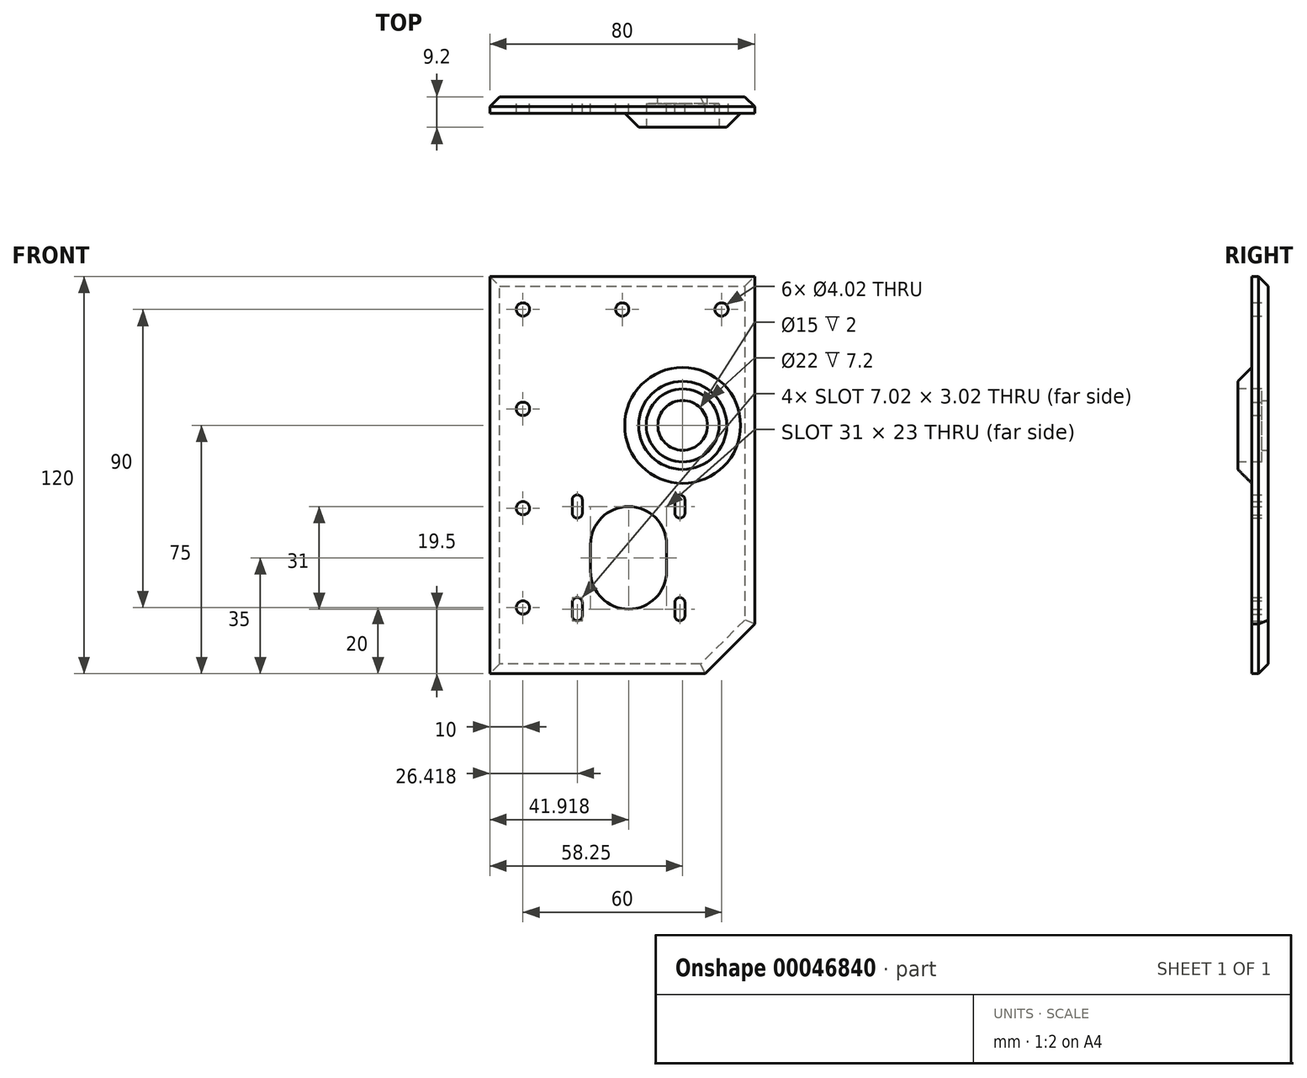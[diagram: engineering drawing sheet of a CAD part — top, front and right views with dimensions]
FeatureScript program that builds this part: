
annotation { "Feature Type Name" : "Feature", "Feature Type Description" : "" }
export const myFeature = defineFeature(function(context is Context, id is Id, definition is map)
    precondition{}
    {
        {
            var Q0;
            Q0=qCreatedBy(makeId("Front.planeOp"),FACE);
            var sketch = newSketch(context, id + "F0", { "sketchPlane" : qUnion([Q0])});
            skLineSegment(sketch, "E0", {"start": v(0, 0) * mm, "end": v(0, 70) * mm});
            skLineSegment(sketch, "E1", {"start": v(0, 70) * mm, "end": v(80, 70) * mm});
            skPoint(sketch, "E2.endSnap0", {"position": v(0, 35) * mm});
            skCircle(sketch, "E3", {"center": v(58.25, 25) * mm, "radius": 7.5 * mm});
            skLineSegment(sketch, "E4", {"start": v(80, 70) * mm, "end": v(80, -35) * mm});
            skLineSegment(sketch, "E5", {"start": v(65, -50) * mm, "end": v(0, -50) * mm});
            skLineSegment(sketch, "E6", {"start": v(0, -50) * mm, "end": v(0, 0) * mm});
            skLineSegment(sketch, "E7", {"start": v(65, -50) * mm, "end": v(80, -35) * mm});
            skLineSegment(sketch, "E8", {"start": v(20, 50) * mm, "end": v(20, -50) * mm, "construction": true});
            skLineSegment(sketch, "E9", {"start": v(20, 50) * mm, "end": v(80, 50) * mm, "construction": true});
            skCircle(sketch, "E10", {"center": v(41.92, -15) * mm, "radius": 11.5 * mm, "construction": true});
            skLineSegment(sketch, "E11", {"start": v(41.92, -15) * mm, "end": v(41.92, 0.5) * mm, "construction": true});
            skLineSegment(sketch, "E12", {"start": v(41.92, 0.5) * mm, "end": v(57.42, 0.5) * mm, "construction": true});
            skLineSegment(sketch, "E13", {"start": v(41.92, 0.5) * mm, "end": v(26.42, 0.5) * mm, "construction": true});
            skLineSegment(sketch, "E14", {"start": v(26.42, 0.5) * mm, "end": v(26.42, -15) * mm, "construction": true});
            skLineSegment(sketch, "E15", {"start": v(26.42, -15) * mm, "end": v(41.92, -15) * mm, "construction": true});
            skLineSegment(sketch, "E16", {"start": v(26.42, -15) * mm, "end": v(26.42, -30.5) * mm, "construction": true});
            skLineSegment(sketch, "E17", {"start": v(26.42, -30.5) * mm, "end": v(41.92, -30.5) * mm, "construction": true});
            skLineSegment(sketch, "E18", {"start": v(41.92, -30.5) * mm, "end": v(41.92, -15) * mm, "construction": true});
            skLineSegment(sketch, "E19", {"start": v(41.92, -15) * mm, "end": v(57.42, -15) * mm, "construction": true});
            skLineSegment(sketch, "E20", {"start": v(57.42, -15) * mm, "end": v(57.42, -30.5) * mm, "construction": true});
            skLineSegment(sketch, "E21", {"start": v(57.42, -30.5) * mm, "end": v(41.92, -30.5) * mm, "construction": true});
            skLineSegment(sketch, "E22", {"start": v(57.42, 0.5) * mm, "end": v(57.42, -15) * mm, "construction": true});
            skLineSegment(sketch, "E23", {"start": v(26.42, 0.5) * mm, "end": v(26.42, 5.5) * mm, "construction": true});
            skLineSegment(sketch, "E24", {"start": v(26.42, 0.5) * mm, "end": v(21.42, 0.5) * mm, "construction": true});
            skLineSegment(sketch, "E25", {"start": v(57.42, 0.5) * mm, "end": v(57.42, 5.5) * mm, "construction": true});
            skLineSegment(sketch, "E26", {"start": v(57.42, 0.5) * mm, "end": v(62.42, 0.5) * mm, "construction": true});
            skLineSegment(sketch, "E27", {"start": v(57.42, -30.5) * mm, "end": v(57.42, -35.5) * mm, "construction": true});
            skLineSegment(sketch, "E28", {"start": v(57.42, -30.5) * mm, "end": v(62.42, -30.5) * mm, "construction": true});
            skLineSegment(sketch, "E29", {"start": v(26.42, -30.5) * mm, "end": v(21.42, -30.5) * mm, "construction": true});
            skLineSegment(sketch, "E30", {"start": v(26.42, -30.5) * mm, "end": v(26.42, -35.5) * mm, "construction": true});
            skArc(sketch, "E31", {"start": v(58.93, -28.5) * mm, "mid": v(57.42, -26.99) * mm, "end": v(55.9, -28.5) * mm});
            skArc(sketch, "E32", {"start": v(55.9, -1.5) * mm, "mid": v(57.42, -3) * mm, "end": v(58.93, -1.5) * mm});
            skArc(sketch, "E33", {"start": v(24.9, -1.5) * mm, "mid": v(26.42, -3) * mm, "end": v(27.93, -1.5) * mm});
            skArc(sketch, "E34", {"start": v(27.93, -28.5) * mm, "mid": v(26.42, -26.99) * mm, "end": v(24.9, -28.5) * mm});
            skArc(sketch, "E35", {"start": v(24.9, -32.5) * mm, "mid": v(26.42, -34) * mm, "end": v(27.93, -32.5) * mm});
            skArc(sketch, "E36", {"start": v(55.9, -32.5) * mm, "mid": v(57.42, -34) * mm, "end": v(58.93, -32.5) * mm});
            skArc(sketch, "E37", {"start": v(58.93, 2.5) * mm, "mid": v(57.42, 4.01) * mm, "end": v(55.9, 2.5) * mm});
            skArc(sketch, "E38", {"start": v(27.93, 2.5) * mm, "mid": v(26.42, 4.01) * mm, "end": v(24.9, 2.5) * mm});
            skArc(sketch, "E39", {"start": v(53.42, -11) * mm, "mid": v(41.92, 0.5) * mm, "end": v(30.42, -11) * mm});
            skCircle(sketch, "E40", {"center": v(10, 60) * mm, "radius": 2 * mm});
            skCircle(sketch, "E41", {"center": v(40, 60) * mm, "radius": 2 * mm});
            skCircle(sketch, "E42", {"center": v(70, 60) * mm, "radius": 2 * mm});
            skCircle(sketch, "E43", {"center": v(10, 30) * mm, "radius": 2 * mm});
            skCircle(sketch, "E44", {"center": v(10, 0) * mm, "radius": 2 * mm});
            skCircle(sketch, "E45", {"center": v(10, -30) * mm, "radius": 2 * mm});
            skLineSegment(sketch, "E46", {"start": v(26.42, 2.5) * mm, "end": v(27.93, 2.5) * mm, "construction": true});
            skLineSegment(sketch, "E47", {"start": v(27.93, 2.5) * mm, "end": v(27.93, -1.5) * mm});
            skLineSegment(sketch, "E48", {"start": v(27.93, -1.5) * mm, "end": v(26.42, -1.5) * mm, "construction": true});
            skLineSegment(sketch, "E49", {"start": v(26.42, -1.5) * mm, "end": v(24.9, -1.5) * mm, "construction": true});
            skLineSegment(sketch, "E50", {"start": v(24.9, -1.5) * mm, "end": v(24.9, 2.5) * mm});
            skLineSegment(sketch, "E51", {"start": v(24.9, 2.5) * mm, "end": v(26.42, 2.5) * mm, "construction": true});
            skLineSegment(sketch, "E52", {"start": v(57.42, 2.5) * mm, "end": v(55.9, 2.5) * mm, "construction": true});
            skLineSegment(sketch, "E53", {"start": v(55.9, 2.5) * mm, "end": v(55.9, -1.5) * mm});
            skLineSegment(sketch, "E54", {"start": v(55.9, -1.5) * mm, "end": v(57.42, -1.5) * mm, "construction": true});
            skLineSegment(sketch, "E55", {"start": v(57.42, -1.5) * mm, "end": v(58.93, -1.5) * mm, "construction": true});
            skLineSegment(sketch, "E56", {"start": v(58.93, -1.5) * mm, "end": v(58.93, 2.5) * mm});
            skLineSegment(sketch, "E57", {"start": v(58.93, 2.5) * mm, "end": v(57.42, 2.5) * mm, "construction": true});
            skLineSegment(sketch, "E58", {"start": v(57.42, -32.5) * mm, "end": v(58.93, -32.5) * mm, "construction": true});
            skLineSegment(sketch, "E59", {"start": v(58.93, -32.5) * mm, "end": v(58.93, -28.5) * mm});
            skLineSegment(sketch, "E60", {"start": v(58.93, -28.5) * mm, "end": v(57.42, -28.5) * mm, "construction": true});
            skLineSegment(sketch, "E61", {"start": v(57.42, -28.5) * mm, "end": v(55.9, -28.5) * mm, "construction": true});
            skLineSegment(sketch, "E62", {"start": v(55.9, -28.5) * mm, "end": v(55.9, -32.5) * mm});
            skLineSegment(sketch, "E63", {"start": v(55.9, -32.5) * mm, "end": v(57.42, -32.5) * mm, "construction": true});
            skLineSegment(sketch, "E64", {"start": v(41.92, -11) * mm, "end": v(53.42, -11) * mm, "construction": true});
            skLineSegment(sketch, "E65", {"start": v(41.92, -19) * mm, "end": v(53.42, -19) * mm});
            skLineSegment(sketch, "E66", {"start": v(41.92, -19) * mm, "end": v(30.42, -19) * mm, "construction": true});
            skLineSegment(sketch, "E67", {"start": v(41.92, -11) * mm, "end": v(30.42, -11) * mm, "construction": true});
            skLineSegment(sketch, "E68", {"start": v(30.42, -11) * mm, "end": v(30.42, -19) * mm});
            skLineSegment(sketch, "E69", {"start": v(53.42, -11) * mm, "end": v(53.42, -19) * mm});
            skLineSegment(sketch, "E70", {"start": v(26.42, -28.5) * mm, "end": v(27.93, -28.5) * mm, "construction": true});
            skLineSegment(sketch, "E71", {"start": v(26.42, -32.5) * mm, "end": v(27.93, -32.5) * mm, "construction": true});
            skLineSegment(sketch, "E72", {"start": v(26.42, -28.5) * mm, "end": v(24.9, -28.5) * mm, "construction": true});
            skLineSegment(sketch, "E73", {"start": v(26.42, -32.5) * mm, "end": v(24.9, -32.5) * mm, "construction": true});
            skLineSegment(sketch, "E74", {"start": v(27.93, -28.5) * mm, "end": v(27.93, -32.5) * mm});
            skLineSegment(sketch, "E75", {"start": v(24.9, -32.5) * mm, "end": v(24.9, -28.5) * mm});
            skArc(sketch, "E76.trimOffspring", {"start": v(30.42, -19) * mm, "mid": v(41.92, -30.5) * mm, "end": v(53.42, -19) * mm});
            skSolve(sketch);
        }
        {
            var Q0;
            Q0=qSketchRegion(id+"F0",true);
            extrude(context, id + "F1", {"entities" : qUnion([Q0]), "depth" : 5 * mm});
        }
        {
            var Q0;
            Q0=makeQuery(id+"F1.opExtrude","CAP_EDGE",EDGE,{"disambiguationData":[OSD([sQuery(id+"F0.wireOp",EDGE,"E4")])],"isStart":true});
            var Q1;
            Q1=makeQuery(id+"F1.opExtrude","CAP_EDGE",EDGE,{"disambiguationData":[OSD([sQuery(id+"F0.wireOp",EDGE,"E1")])],"isStart":true});
            var Q2;
            Q2=makeQuery(id+"F1.opExtrude","CAP_EDGE",EDGE,{"disambiguationData":[OSD([sQuery(id+"F0.wireOp",EDGE,"E0"),sQuery(id+"F0.wireOp",EDGE,"E6")])],"isStart":true});
            var Q3;
            Q3=makeQuery(id+"F1.opExtrude","CAP_EDGE",EDGE,{"disambiguationData":[OSD([sQuery(id+"F0.wireOp",EDGE,"E5")])],"isStart":true});
            var Q4;
            Q4=makeQuery(id+"F1.opExtrude","CAP_EDGE",EDGE,{"disambiguationData":[OSD([sQuery(id+"F0.wireOp",EDGE,"E7")])],"isStart":true});
            chamfer(context, id + "F2", {"entities" : qUnion([Q0, Q1, Q2, Q3, Q4]), "width" : 3 * mm, "tangentPropagation" : true});
        }
        {
            var Q0;
            Q0=makeQuery(id+"F1.opExtrude","CAP_FACE",FACE,{"disambiguationData":[OSD([sQuery(id+"F0.wireOp",EDGE,"E0"),sQuery(id+"F0.wireOp",EDGE,"E1"),sQuery(id+"F0.wireOp",EDGE,"E3"),sQuery(id+"F0.wireOp",EDGE,"E4"),sQuery(id+"F0.wireOp",EDGE,"E5"),sQuery(id+"F0.wireOp",EDGE,"E6"),sQuery(id+"F0.wireOp",EDGE,"E7"),sQuery(id+"F0.wireOp",EDGE,"E31"),sQuery(id+"F0.wireOp",EDGE,"E32"),sQuery(id+"F0.wireOp",EDGE,"E33"),sQuery(id+"F0.wireOp",EDGE,"E34"),sQuery(id+"F0.wireOp",EDGE,"E35"),sQuery(id+"F0.wireOp",EDGE,"E36"),sQuery(id+"F0.wireOp",EDGE,"E37"),sQuery(id+"F0.wireOp",EDGE,"E38"),sQuery(id+"F0.wireOp",EDGE,"E39"),sQuery(id+"F0.wireOp",EDGE,"E40"),sQuery(id+"F0.wireOp",EDGE,"E41"),sQuery(id+"F0.wireOp",EDGE,"E42"),sQuery(id+"F0.wireOp",EDGE,"E43"),sQuery(id+"F0.wireOp",EDGE,"E44"),sQuery(id+"F0.wireOp",EDGE,"E45"),sQuery(id+"F0.wireOp",EDGE,"E47"),sQuery(id+"F0.wireOp",EDGE,"E50"),sQuery(id+"F0.wireOp",EDGE,"E53"),sQuery(id+"F0.wireOp",EDGE,"E56"),sQuery(id+"F0.wireOp",EDGE,"E59"),sQuery(id+"F0.wireOp",EDGE,"E62"),sQuery(id+"F0.wireOp",EDGE,"E68"),sQuery(id+"F0.wireOp",EDGE,"E69"),sQuery(id+"F0.wireOp",EDGE,"E74"),sQuery(id+"F0.wireOp",EDGE,"E75"),sQuery(id+"F0.wireOp",EDGE,"E76.trimOffspring")])],"isStart":false});
            var sketch = newSketch(context, id + "F3", { "sketchPlane" : qUnion([Q0])});
            skCircle(sketch, "E77", {"center": v(58.25, 25) * mm, "radius": 11 * mm});
            skSolve(sketch);
        }
        {
            var Q0;
            Q0=qSketchRegion(id+"F3",true);
            extrude(context, id + "F4", {"entities" : qUnion([Q0]), "operationType" : NewBodyOperationType.REMOVE, "oppositeDirection" : true, "depth" : 3 * mm});
        }
        {
            var Q0;
            Q0=makeQuery(id+"F1.opExtrude","CAP_FACE",FACE,{"disambiguationData":[OSD([sQuery(id+"F0.wireOp",EDGE,"E0"),sQuery(id+"F0.wireOp",EDGE,"E1"),sQuery(id+"F0.wireOp",EDGE,"E3"),sQuery(id+"F0.wireOp",EDGE,"E4"),sQuery(id+"F0.wireOp",EDGE,"E5"),sQuery(id+"F0.wireOp",EDGE,"E6"),sQuery(id+"F0.wireOp",EDGE,"E7"),sQuery(id+"F0.wireOp",EDGE,"E31"),sQuery(id+"F0.wireOp",EDGE,"E32"),sQuery(id+"F0.wireOp",EDGE,"E33"),sQuery(id+"F0.wireOp",EDGE,"E34"),sQuery(id+"F0.wireOp",EDGE,"E35"),sQuery(id+"F0.wireOp",EDGE,"E36"),sQuery(id+"F0.wireOp",EDGE,"E37"),sQuery(id+"F0.wireOp",EDGE,"E38"),sQuery(id+"F0.wireOp",EDGE,"E39"),sQuery(id+"F0.wireOp",EDGE,"E40"),sQuery(id+"F0.wireOp",EDGE,"E41"),sQuery(id+"F0.wireOp",EDGE,"E42"),sQuery(id+"F0.wireOp",EDGE,"E43"),sQuery(id+"F0.wireOp",EDGE,"E44"),sQuery(id+"F0.wireOp",EDGE,"E45"),sQuery(id+"F0.wireOp",EDGE,"E47"),sQuery(id+"F0.wireOp",EDGE,"E50"),sQuery(id+"F0.wireOp",EDGE,"E53"),sQuery(id+"F0.wireOp",EDGE,"E56"),sQuery(id+"F0.wireOp",EDGE,"E59"),sQuery(id+"F0.wireOp",EDGE,"E62"),sQuery(id+"F0.wireOp",EDGE,"E68"),sQuery(id+"F0.wireOp",EDGE,"E69"),sQuery(id+"F0.wireOp",EDGE,"E74"),sQuery(id+"F0.wireOp",EDGE,"E75"),sQuery(id+"F0.wireOp",EDGE,"E76.trimOffspring")])],"isStart":false});
            var sketch = newSketch(context, id + "F5", { "sketchPlane" : qUnion([Q0])});
            skCircle(sketch, "E78", {"center": v(58.25, 25) * mm, "radius": 17.5 * mm});
            skCircle(sketch, "E79", {"center": v(58.25, 25) * mm, "radius": 11 * mm});
            skSolve(sketch);
        }
        {
            var Q0;
            Q0=qSketchRegion(id+"F5",true);
            extrude(context, id + "F6", {"entities" : qUnion([Q0]), "operationType" : NewBodyOperationType.ADD, "depth" : 4.2 * mm});
        }
        {
            var Q0;
            Q0=makeQuery(id+"F6.opExtrude","CAP_EDGE",EDGE,{"disambiguationData":[OSD([sQuery(id+"F5.wireOp",EDGE,"E78")])],"isStart":false});
            chamfer(context, id + "F7", {"entities" : qUnion([Q0]), "width" : 4.2 * mm, "tangentPropagation" : true});
        }
    });
